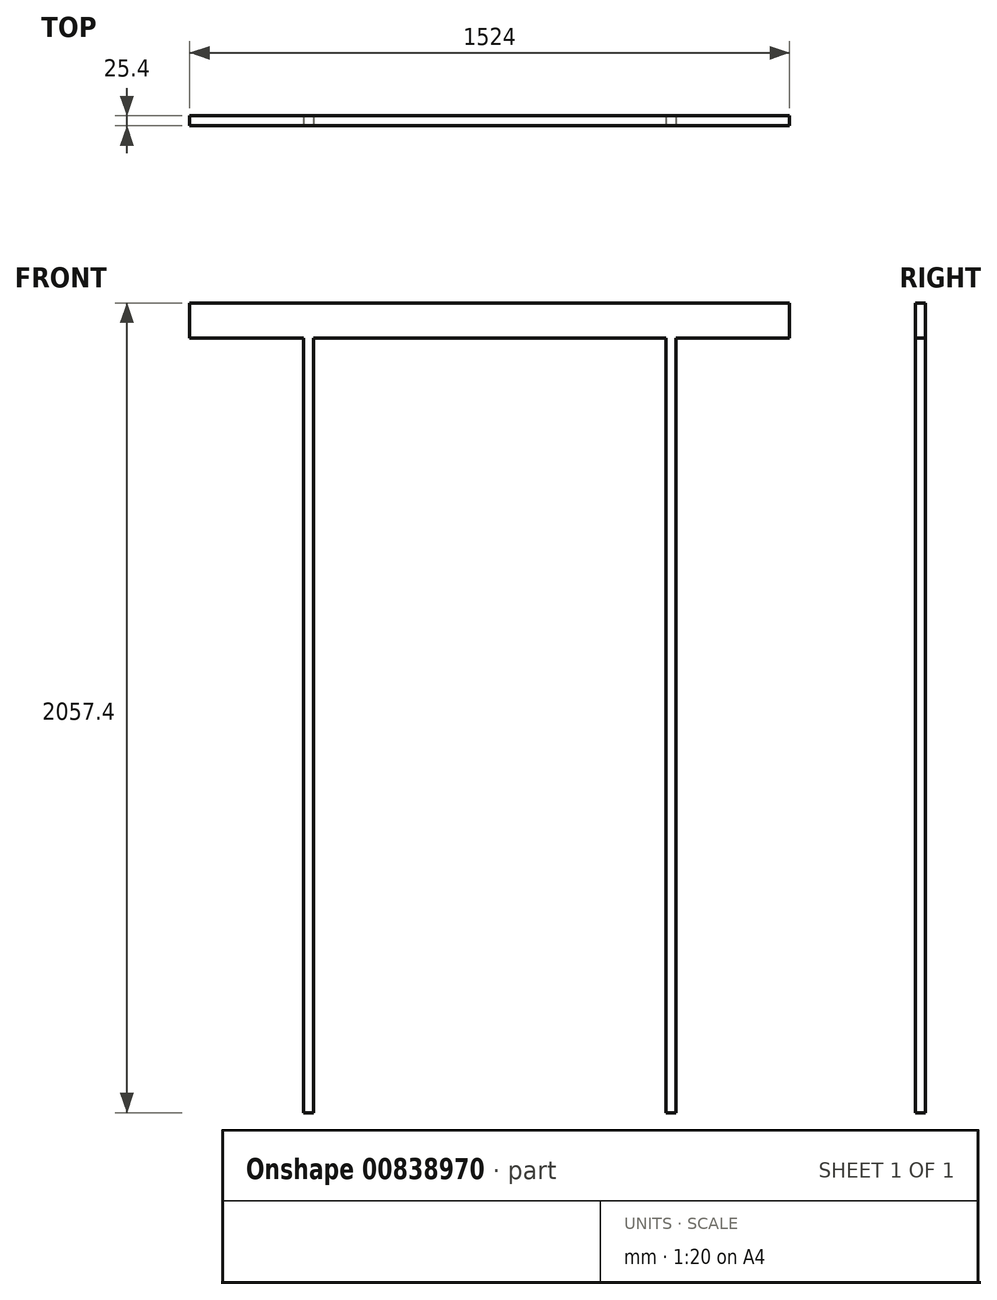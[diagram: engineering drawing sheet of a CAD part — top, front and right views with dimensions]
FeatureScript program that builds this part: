
annotation { "Feature Type Name" : "Feature", "Feature Type Description" : "" }
export const myFeature = defineFeature(function(context is Context, id is Id, definition is map)
    precondition{}
    {
        {
            var Q0;
            Q0=qCreatedBy(makeId("Front.planeOp"),FACE);
            var sketch = newSketch(context, id + "F0", { "sketchPlane" : qUnion([Q0])});
            skLineSegment(sketch, "E0", {"start": v(-447.67, -2057.4) * mm, "end": v(-447.68, -88.9) * mm});
            skLineSegment(sketch, "E1", {"start": v(-447.68, -88.9) * mm, "end": v(0, -88.9) * mm});
            skLineSegment(sketch, "E2", {"start": v(0, 0) * mm, "end": v(0, -2057.4) * mm, "construction": true});
            skLineSegment(sketch, "E3", {"start": v(-762, 0) * mm, "end": v(0, 0) * mm});
            skLineSegment(sketch, "E4", {"start": v(-447.67, -2057.4) * mm, "end": v(-473.07, -2057.4) * mm});
            skLineSegment(sketch, "E5.MirrorCS", {"start": v(447.68, -88.9) * mm, "end": v(0, -88.9) * mm});
            skLineSegment(sketch, "E6.MirrorCS", {"start": v(762, 0) * mm, "end": v(0, 0) * mm});
            skLineSegment(sketch, "E7.MirrorCS", {"start": v(447.67, -2057.4) * mm, "end": v(447.68, -88.9) * mm});
            skLineSegment(sketch, "E8.MirrorCS", {"start": v(447.67, -2057.4) * mm, "end": v(473.07, -2057.4) * mm});
            skLineSegment(sketch, "E9", {"start": v(-473.07, -2057.4) * mm, "end": v(-473.07, -88.9) * mm});
            skLineSegment(sketch, "E10", {"start": v(-473.07, -88.9) * mm, "end": v(-762, -88.9) * mm});
            skLineSegment(sketch, "E11", {"start": v(-762, 0) * mm, "end": v(-762, -88.9) * mm});
            skLineSegment(sketch, "E12.MirrorCS", {"start": v(473.07, -88.9) * mm, "end": v(762, -88.9) * mm});
            skLineSegment(sketch, "E13.MirrorCS", {"start": v(762, 0) * mm, "end": v(762, -88.9) * mm});
            skLineSegment(sketch, "E14.MirrorCS", {"start": v(473.07, -2057.4) * mm, "end": v(473.07, -88.9) * mm});
            skSolve(sketch);
        }
        {
            var Q0;
            Q0=makeQuery(id+"F0.imprint","IMPRINT",FACE,{"disambiguationData":[TD([[makeQuery(id+"F0.imprint","IMPRINT",EDGE,{"derivedFrom":sQuery(id+"F0.wireOp",EDGE,"E0")}),1.0]])]});
            extrude(context, id + "F1", {"entities" : qUnion([Q0]), "oppositeDirection" : true, "depth" : 25.4 * mm, "offsetDistance" : 25.4 * mm});
        }
    });
